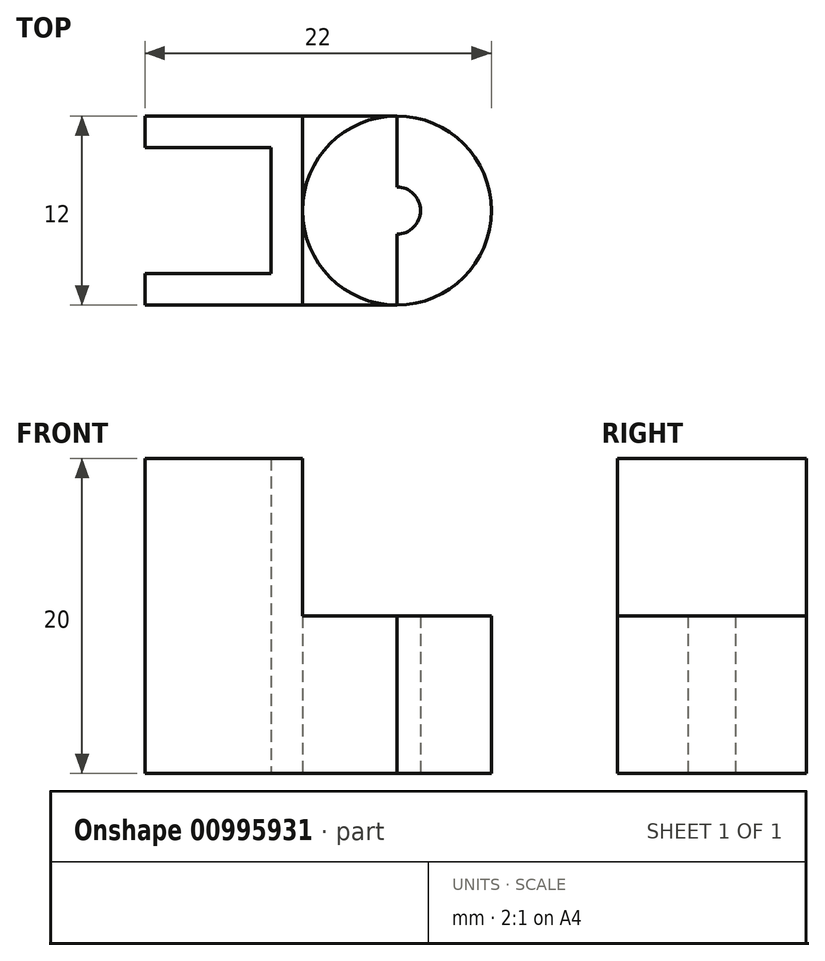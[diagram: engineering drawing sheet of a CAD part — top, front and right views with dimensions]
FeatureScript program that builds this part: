
annotation { "Feature Type Name" : "Feature", "Feature Type Description" : "" }
export const myFeature = defineFeature(function(context is Context, id is Id, definition is map)
    precondition{}
    {
        {
            var Q0;
            Q0=qCreatedBy(makeId("Top.planeOp"),FACE);
            var sketch = newSketch(context, id + "F0", { "sketchPlane" : qUnion([Q0])});
            skLineSegment(sketch, "E0", {"start": v(0, 0) * mm, "end": v(8, 0) * mm});
            skLineSegment(sketch, "E1", {"start": v(8, 0) * mm, "end": v(8, 8) * mm});
            skLineSegment(sketch, "E2", {"start": v(8, 8) * mm, "end": v(0, 8) * mm});
            skLineSegment(sketch, "E3", {"start": v(0, 0) * mm, "end": v(0, 8) * mm});
            skLineSegment(sketch, "E4.0", {"start": v(10, 10) * mm, "end": v(0, 10) * mm});
            skLineSegment(sketch, "E4.2", {"start": v(0, -2) * mm, "end": v(10, -2) * mm});
            skLineSegment(sketch, "E5", {"start": v(10, 10) * mm, "end": v(16, 10) * mm});
            skLineSegment(sketch, "E6", {"start": v(16, 10) * mm, "end": v(16, -2) * mm});
            skLineSegment(sketch, "E7", {"start": v(10, -2) * mm, "end": v(16, -2) * mm});
            skArc(sketch, "E8", {"start": v(16, -2) * mm, "mid": v(22, 4) * mm, "end": v(16, 10) * mm});
            skCircle(sketch, "E9", {"center": v(16, 4) * mm, "radius": 1.5 * mm});
            skLineSegment(sketch, "E10", {"start": v(0, 10) * mm, "end": v(0, 8) * mm});
            skLineSegment(sketch, "E11", {"start": v(0, 0) * mm, "end": v(0, -2) * mm});
            skArc(sketch, "E12", {"start": v(16, 10) * mm, "mid": v(10, 4) * mm, "end": v(16, -2) * mm});
            skLineSegment(sketch, "E13", {"start": v(10, -2) * mm, "end": v(10, 10) * mm});
            skSolve(sketch);
        }
        {
            var Q0;
            Q0=makeQuery(id+"F0.imprint","IMPRINT",FACE,{"disambiguationData":[TD([[makeQuery(id+"F0.imprint","IMPRINT",EDGE,{"derivedFrom":sQuery(id+"F0.wireOp",EDGE,"E0")}),-1.0]])]});
            var Q1;
            Q1=makeQuery(id+"F0.imprint","IMPRINT",FACE,{"disambiguationData":[TD([[makeQuery(id+"F0.imprint","IMPRINT",EDGE,{"derivedFrom":sQuery(id+"F0.wireOp",EDGE,"E4.1")}),-1.0]])]});
            var Q2;
            {var subQ1=sQuery(id+"F0.wireOp",EDGE,"E8");Q2=makeQuery(id+"F0.imprint","IMPRINT",FACE,{"disambiguationData":[TD([[makeQuery(id+"F0.imprint","IMPRINT",EDGE,{"derivedFrom":subQ1}),1.0]])]});}
            var Q3;
            {var subQ2=sQuery(id+"F0.wireOp",EDGE,"E6");var subQ6=sQuery(id+"F0.wireOp",EDGE,"E9");var subQ8=makeQuery(id+"F0.imprint","INTERSECT",VERTEX,{"disambiguationData":[OD(0.0)],"derivedFrom":[subQ2,subQ6]});Q3=makeQuery(id+"F0.imprint","IMPRINT",FACE,{"disambiguationData":[TD([[makeQuery(id+"F0.imprint","IMPRINT",EDGE,{"disambiguationData":[TD([[subQ8,-1.0]])],"derivedFrom":subQ6}),-1.0]])]});}
            var Q4;
            {var subQ0=sQuery(id+"F0.wireOp",EDGE,"55ea673d-e93c-4888-aa08-729aeeb4521a.trimOffspring");Q4=makeQuery(id+"F0.imprint","IMPRINT",FACE,{"disambiguationData":[TD([[makeQuery(id+"F0.imprint","IMPRINT",EDGE,{"derivedFrom":subQ0}),-1.0]])]});}
            var Q5;
            {var subQ4=sQuery(id+"F0.wireOp",EDGE,"E12");Q5=makeQuery(id+"F0.imprint","IMPRINT",FACE,{"disambiguationData":[TD([[makeQuery(id+"F0.imprint","IMPRINT",EDGE,{"derivedFrom":subQ4}),-1.0]])]});}
            extrude(context, id + "F1", {"entities" : qUnion([Q0, Q1, Q2, Q3, Q4, Q5]), "depth" : 20 * mm, "offsetDistance" : 25 * mm});
        }
        {
            var Q0;
            {var subQ1=sQuery(id+"F0.wireOp",EDGE,"E8");Q0=makeQuery(id+"F0.imprint","IMPRINT",FACE,{"disambiguationData":[TD([[makeQuery(id+"F0.imprint","IMPRINT",EDGE,{"derivedFrom":subQ1}),1.0]])]});}
            var Q1;
            {var subQ2=sQuery(id+"F0.wireOp",EDGE,"E6");var subQ6=sQuery(id+"F0.wireOp",EDGE,"E9");var subQ8=makeQuery(id+"F0.imprint","INTERSECT",VERTEX,{"disambiguationData":[OD(0.0)],"derivedFrom":[subQ2,subQ6]});Q1=makeQuery(id+"F0.imprint","IMPRINT",FACE,{"disambiguationData":[TD([[makeQuery(id+"F0.imprint","IMPRINT",EDGE,{"disambiguationData":[TD([[subQ8,-1.0]])],"derivedFrom":subQ6}),-1.0]])]});}
            var Q2;
            Q2=makeQuery(id+"F1.opExtrude","CAP_FACE",FACE,{"disambiguationData":[OSD([sQuery(id+"F0.wireOp",EDGE,"E0"),sQuery(id+"F0.wireOp",EDGE,"E1"),sQuery(id+"F0.wireOp",EDGE,"E2"),sQuery(id+"F0.wireOp",EDGE,"E4.0"),sQuery(id+"F0.wireOp",EDGE,"E4.2"),sQuery(id+"F0.wireOp",EDGE,"E5"),sQuery(id+"F0.wireOp",EDGE,"E7"),sQuery(id+"F0.wireOp",EDGE,"E8"),sQuery(id+"F0.wireOp",EDGE,"E9"),sQuery(id+"F0.wireOp",EDGE,"E10"),sQuery(id+"F0.wireOp",EDGE,"E11")])],"isStart":false});
            var Q3;
            {var subQ0=sQuery(id+"F0.wireOp",EDGE,"E7");Q3=makeQuery(id+"F0.imprint","IMPRINT",FACE,{"disambiguationData":[TD([[makeQuery(id+"F0.imprint","IMPRINT",EDGE,{"derivedFrom":subQ0}),1.0]])]});}
            var Q4;
            {var subQ0=sQuery(id+"F0.wireOp",EDGE,"E5");Q4=makeQuery(id+"F0.imprint","IMPRINT",FACE,{"disambiguationData":[TD([[makeQuery(id+"F0.imprint","IMPRINT",EDGE,{"derivedFrom":subQ0}),-1.0]])]});}
            extrude(context, id + "F2", {"entities" : qUnion([Q0, Q1, Q2, Q3, Q4]), "operationType" : NewBodyOperationType.REMOVE, "depth" : 20 * mm, "offsetDistance" : 25 * mm, "hasSecondDirection" : true, "secondDirectionOppositeDirection" : false, "secondDirectionDepth" : 10 * mm});
        }
    });
